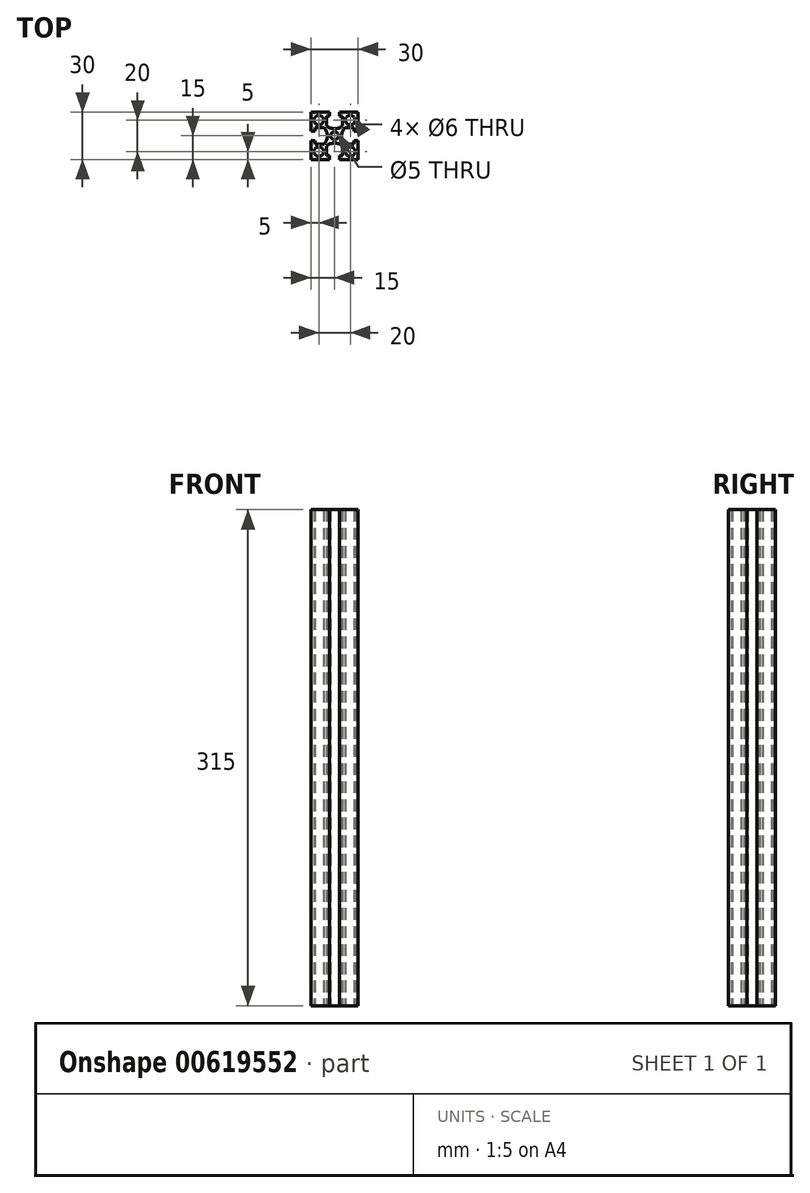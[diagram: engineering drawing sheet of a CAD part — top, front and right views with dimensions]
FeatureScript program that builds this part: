
annotation { "Feature Type Name" : "Feature", "Feature Type Description" : "" }
export const myFeature = defineFeature(function(context is Context, id is Id, definition is map)
    precondition{}
    {
        {
            var Q0;
            Q0=qCreatedBy(makeId("Top.planeOp"),FACE);
            var sketch = newSketch(context, id + "F0", { "sketchPlane" : qUnion([Q0])});
            skCircle(sketch, "E0", {"center": v(-10, 10) * mm, "radius": 3 * mm});
            skCircle(sketch, "E1.MirrorC", {"center": v(-10, -10) * mm, "radius": 3 * mm});
            skLineSegment(sketch, "E2.top", {"start": v(-15, 3.15) * mm, "end": v(-15, -3.15) * mm});
            skLineSegment(sketch, "E2.left", {"start": v(-12.5, 3.15) * mm, "end": v(-15, 3.15) * mm});
            skLineSegment(sketch, "E2.right", {"start": v(-12.5, -3.15) * mm, "end": v(-15, -3.15) * mm});
            skLineSegment(sketch, "E3.bottom", {"start": v(-12.5, 5.15) * mm, "end": v(-12.5, 3.15) * mm});
            skLineSegment(sketch, "E3.left", {"start": v(-12.5, 5.15) * mm, "end": v(-6.55, 5.15) * mm});
            skLineSegment(sketch, "E3.right", {"start": v(-12.5, -5.15) * mm, "end": v(-6.55, -5.15) * mm});
            skArc(sketch, "E4", {"start": v(-6.55, -5.15) * mm, "mid": v(-4.5, 0) * mm, "end": v(-6.55, 5.15) * mm});
            skLineSegment(sketch, "E5.trimOffspring", {"start": v(-12.5, -3.15) * mm, "end": v(-12.5, -5.15) * mm});
            skLineSegment(sketch, "E6.bottom", {"start": v(15, -15) * mm, "end": v(-15, -15) * mm});
            skLineSegment(sketch, "E6.top", {"start": v(15, 15) * mm, "end": v(-15, 15) * mm});
            skLineSegment(sketch, "E6.left", {"start": v(15, -15) * mm, "end": v(15, 15) * mm});
            skLineSegment(sketch, "E6.right", {"start": v(-15, -15) * mm, "end": v(-15, 15) * mm});
            skPoint(sketch, "E6.middle", {"position": v(0, 0) * mm});
            skCircle(sketch, "E7.MirrorC", {"center": v(10, 10) * mm, "radius": 3 * mm});
            skCircle(sketch, "E8.MirrorC", {"center": v(10, -10) * mm, "radius": 3 * mm});
            skLineSegment(sketch, "E9.1.0", {"start": v(-5.15, -12.5) * mm, "end": v(-3.15, -12.5) * mm});
            skArc(sketch, "E9.1.1", {"start": v(5.15, -6.55) * mm, "mid": v(0, -4.5) * mm, "end": v(-5.15, -6.55) * mm});
            skLineSegment(sketch, "E9.1.2", {"start": v(-3.15, -15) * mm, "end": v(3.15, -15) * mm});
            skLineSegment(sketch, "E9.1.3", {"start": v(-3.15, -12.5) * mm, "end": v(-3.15, -15) * mm});
            skLineSegment(sketch, "E9.1.4", {"start": v(-5.15, -12.5) * mm, "end": v(-5.15, -6.55) * mm});
            skLineSegment(sketch, "E9.1.5", {"start": v(3.15, -12.5) * mm, "end": v(5.15, -12.5) * mm});
            skLineSegment(sketch, "E9.1.6", {"start": v(5.15, -12.5) * mm, "end": v(5.15, -6.55) * mm});
            skLineSegment(sketch, "E9.1.7", {"start": v(3.15, -12.5) * mm, "end": v(3.15, -15) * mm});
            skLineSegment(sketch, "E9.2.0", {"start": v(12.5, -5.15) * mm, "end": v(12.5, -3.15) * mm});
            skArc(sketch, "E9.2.1", {"start": v(6.55, 5.15) * mm, "mid": v(4.5, 0) * mm, "end": v(6.55, -5.15) * mm});
            skLineSegment(sketch, "E9.2.2", {"start": v(15, -3.15) * mm, "end": v(15, 3.15) * mm});
            skLineSegment(sketch, "E9.2.3", {"start": v(12.5, -3.15) * mm, "end": v(15, -3.15) * mm});
            skLineSegment(sketch, "E9.2.4", {"start": v(12.5, -5.15) * mm, "end": v(6.55, -5.15) * mm});
            skLineSegment(sketch, "E9.2.5", {"start": v(12.5, 3.15) * mm, "end": v(12.5, 5.15) * mm});
            skLineSegment(sketch, "E9.2.6", {"start": v(12.5, 5.15) * mm, "end": v(6.55, 5.15) * mm});
            skLineSegment(sketch, "E9.2.7", {"start": v(12.5, 3.15) * mm, "end": v(15, 3.15) * mm});
            skLineSegment(sketch, "E9.3.0", {"start": v(5.15, 12.5) * mm, "end": v(3.15, 12.5) * mm});
            skArc(sketch, "E9.3.1", {"start": v(-5.15, 6.55) * mm, "mid": v(0, 4.5) * mm, "end": v(5.15, 6.55) * mm});
            skLineSegment(sketch, "E9.3.2", {"start": v(3.15, 15) * mm, "end": v(-3.15, 15) * mm});
            skLineSegment(sketch, "E9.3.3", {"start": v(3.15, 12.5) * mm, "end": v(3.15, 15) * mm});
            skLineSegment(sketch, "E9.3.4", {"start": v(5.15, 12.5) * mm, "end": v(5.15, 6.55) * mm});
            skLineSegment(sketch, "E9.3.5", {"start": v(-3.15, 12.5) * mm, "end": v(-5.15, 12.5) * mm});
            skLineSegment(sketch, "E9.3.6", {"start": v(-5.15, 12.5) * mm, "end": v(-5.15, 6.55) * mm});
            skLineSegment(sketch, "E9.3.7", {"start": v(-3.15, 12.5) * mm, "end": v(-3.15, 15) * mm});
            skCircle(sketch, "E10", {"center": v(0, 0) * mm, "radius": 2.5 * mm});
            skSolve(sketch);
        }
        {
            var Q0;
            Q0=makeQuery(id+"F0.imprint","IMPRINT",FACE,{"disambiguationData":[TD([[makeQuery(id+"F0.imprint","IMPRINT",EDGE,{"derivedFrom":sQuery(id+"F0.wireOp",EDGE,"E0")}),-1.0]])]});
            extrude(context, id + "F1", {"entities" : qUnion([Q0]), "depth" : 315 * mm, "offsetDistance" : 25 * mm});
        }
    });
